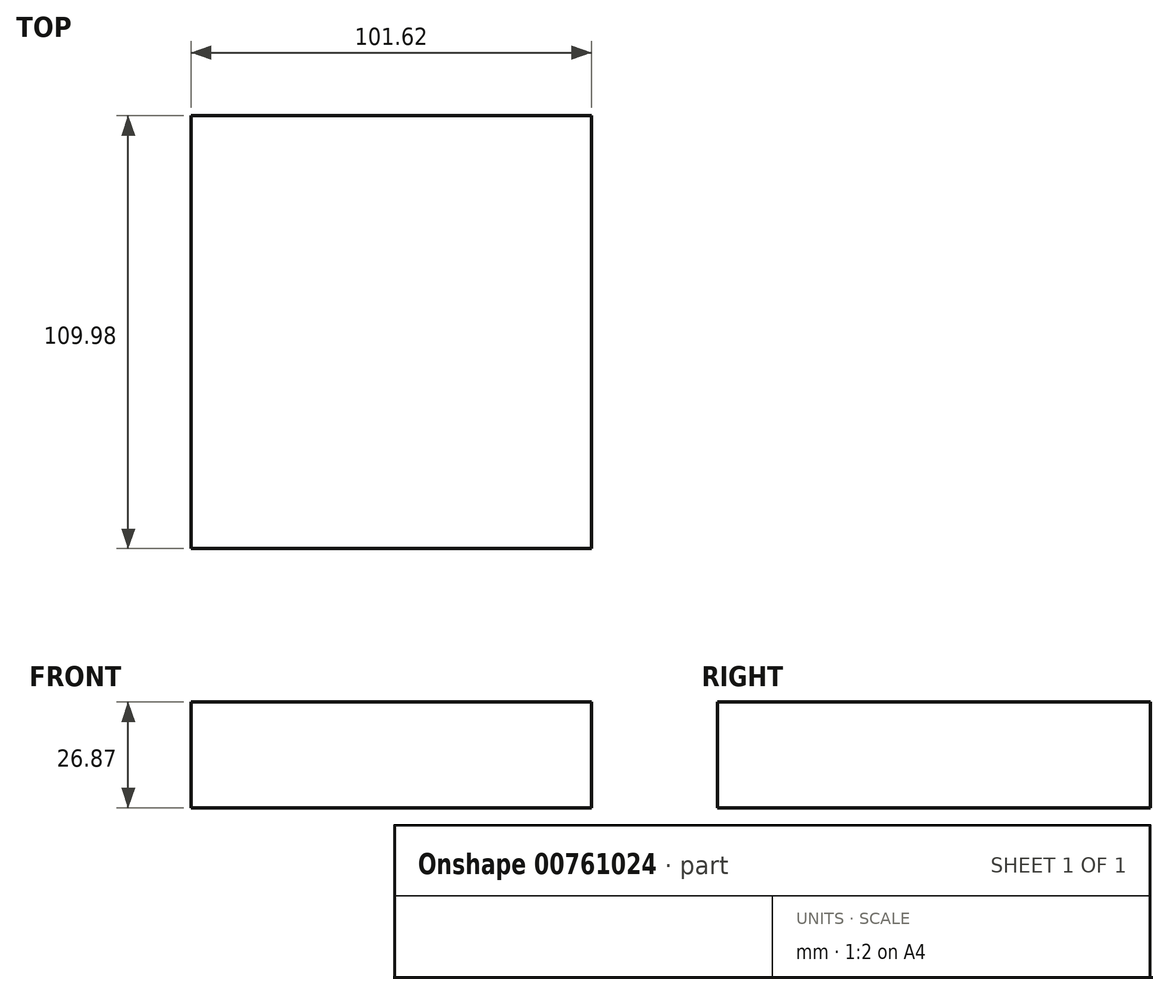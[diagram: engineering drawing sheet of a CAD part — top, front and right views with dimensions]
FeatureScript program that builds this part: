
annotation { "Feature Type Name" : "Feature", "Feature Type Description" : "" }
export const myFeature = defineFeature(function(context is Context, id is Id, definition is map)
    precondition{}
    {
        {
            var Q0;
            Q0=qCreatedBy(makeId("Front.planeOp"),FACE);
            var sketch = newSketch(context, id + "F0", { "sketchPlane" : qUnion([Q0])});
            skLineSegment(sketch, "E0.bottom", {"start": v(-46.04, -5.35) * mm, "end": v(55.58, -5.35) * mm});
            skLineSegment(sketch, "E0.top", {"start": v(-46.04, -32.22) * mm, "end": v(55.58, -32.22) * mm});
            skLineSegment(sketch, "E0.left", {"start": v(-46.04, -5.35) * mm, "end": v(-46.04, -32.22) * mm});
            skLineSegment(sketch, "E0.right", {"start": v(55.58, -5.35) * mm, "end": v(55.58, -32.22) * mm});
            skSolve(sketch);
        }
        {
            var Q0;
            Q0=makeQuery(id+"F0.imprint","IMPRINT",FACE,{"disambiguationData":[TD([[makeQuery(id+"F0.imprint","IMPRINT",EDGE,{"derivedFrom":sQuery(id+"F0.wireOp",EDGE,"E0.bottom")}),-1.0]])]});
            extrude(context, id + "F1", {"entities" : qUnion([Q0]), "depth" : 109.98 * mm, "offsetDistance" : 25.4 * mm});
        }
        {
            var Q0;
            Q0=makeQuery(id+"F1.opExtrude","SWEPT_FACE",FACE,{"disambiguationData":[OSD([sQuery(id+"F0.wireOp",EDGE,"E0.bottom")])]});
            extrude(context, id + "F2", {"entities" : qUnion([Q0]), "operationType" : NewBodyOperationType.ADD, "oppositeDirection" : true, "depth" : 11.68 * mm, "offsetDistance" : 25.4 * mm});
        }
    });
